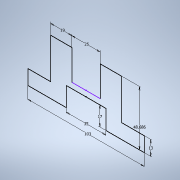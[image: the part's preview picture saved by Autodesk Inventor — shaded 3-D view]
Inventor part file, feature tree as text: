
AUTODESK INVENTOR PART (.ipt)
format: ipt  version: 2022 (Build 260153000, 153)  size: 97,792 bytes
history: native  units: mm
features: sketch x1
ambient origin geometry x8: Origin, YZ Plane, XZ Plane, XY Plane, X Axis, Y Axis, Z Axis, Center Point
feature tree (1):
  sketch  "Esboço1"  dims[d0=103.0mm d1=35.0mm d2=17.0mm d3=13.0mm d4=19.0mm d5=25.0mm d6=48.685638mm]
